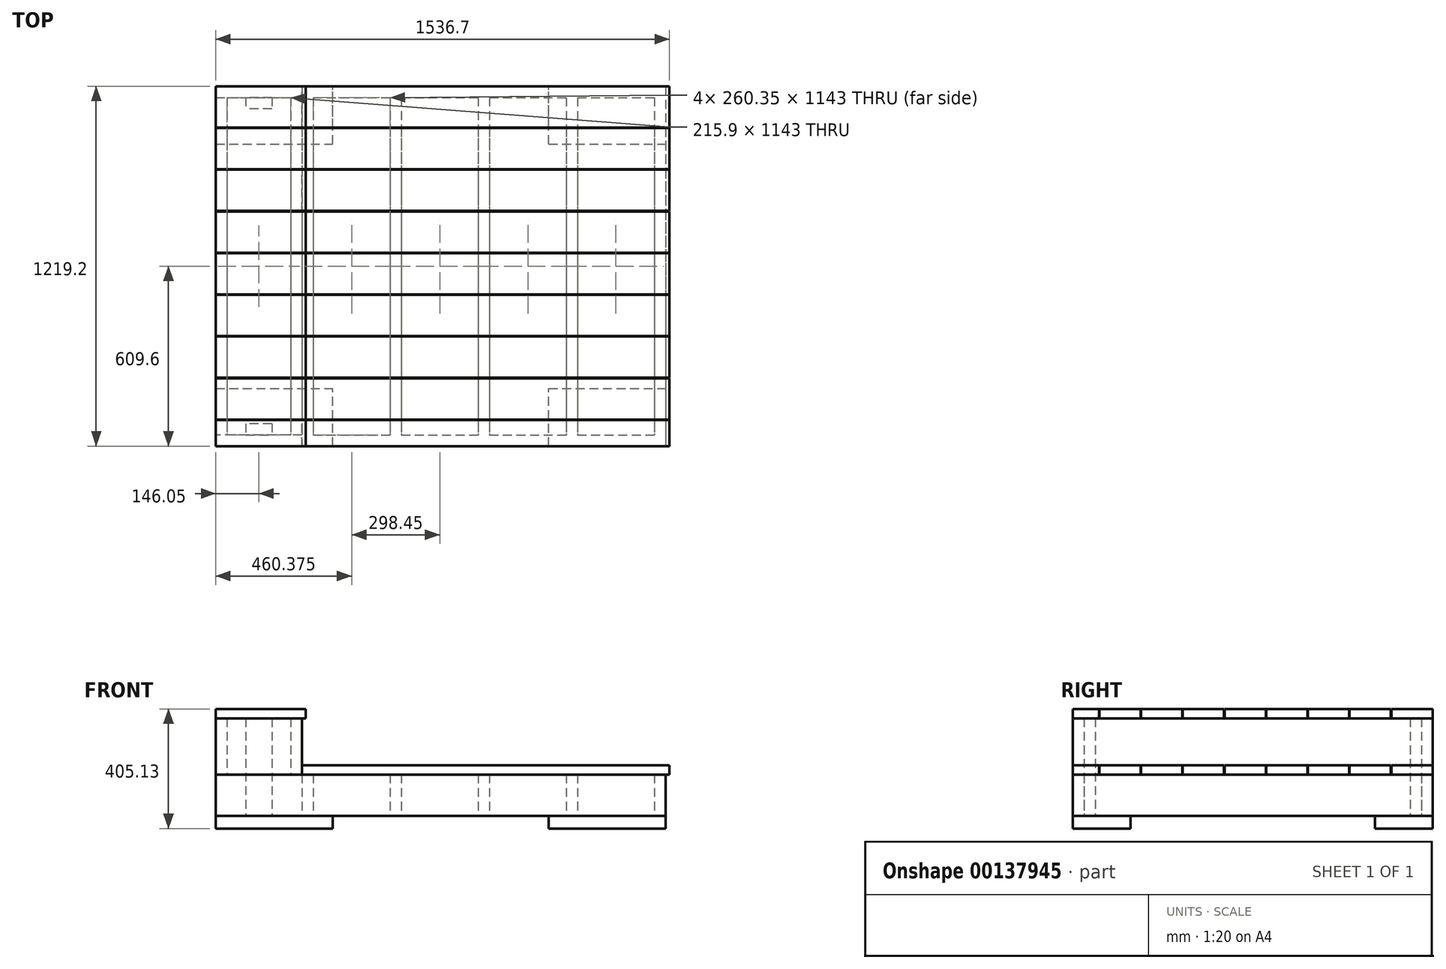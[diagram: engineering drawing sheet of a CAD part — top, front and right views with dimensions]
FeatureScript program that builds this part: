
annotation { "Feature Type Name" : "Feature", "Feature Type Description" : "" }
export const myFeature = defineFeature(function(context is Context, id is Id, definition is map)
    precondition{}
    {
        {
            var Q0;
            Q0=qCreatedBy(makeId("Top.planeOp"),FACE);
            var sketch = newSketch(context, id + "F0", { "sketchPlane" : qUnion([Q0])});
            skLineSegment(sketch, "E0.bottom", {"start": v(-762, 609.6) * mm, "end": v(762, 609.6) * mm});
            skLineSegment(sketch, "E0.top", {"start": v(-762, -609.6) * mm, "end": v(762, -609.6) * mm});
            skLineSegment(sketch, "E0.left", {"start": v(-762, 609.6) * mm, "end": v(-762, 571.5) * mm});
            skLineSegment(sketch, "E0.right", {"start": v(762, 609.6) * mm, "end": v(762, -609.6) * mm});
            skLineSegment(sketch, "E1.bottom", {"start": v(-431.8, 571.5) * mm, "end": v(-171.45, 571.5) * mm});
            skLineSegment(sketch, "E1.top", {"start": v(-431.8, -571.5) * mm, "end": v(-171.45, -571.5) * mm});
            skLineSegment(sketch, "E1.left", {"start": v(-431.8, 571.5) * mm, "end": v(-431.8, -571.5) * mm});
            skLineSegment(sketch, "E1.right", {"start": v(-171.45, 571.5) * mm, "end": v(-171.45, -571.5) * mm});
            skLineSegment(sketch, "E2.bottom", {"start": v(-133.35, 571.5) * mm, "end": v(127, 571.5) * mm});
            skLineSegment(sketch, "E2.top", {"start": v(-133.35, -571.5) * mm, "end": v(127, -571.5) * mm});
            skLineSegment(sketch, "E2.left", {"start": v(-133.35, 571.5) * mm, "end": v(-133.35, -571.5) * mm});
            skLineSegment(sketch, "E2.right", {"start": v(127, 571.5) * mm, "end": v(127, -571.5) * mm});
            skLineSegment(sketch, "E3.bottom", {"start": v(165.1, 571.5) * mm, "end": v(425.45, 571.5) * mm});
            skLineSegment(sketch, "E3.top", {"start": v(165.1, -571.5) * mm, "end": v(425.45, -571.5) * mm});
            skLineSegment(sketch, "E3.left", {"start": v(165.1, 571.5) * mm, "end": v(165.1, -571.5) * mm});
            skLineSegment(sketch, "E3.right", {"start": v(425.45, 571.5) * mm, "end": v(425.45, -571.5) * mm});
            skLineSegment(sketch, "E4.bottom", {"start": v(463.55, 571.5) * mm, "end": v(723.9, 571.5) * mm});
            skLineSegment(sketch, "E4.top", {"start": v(463.55, -571.5) * mm, "end": v(723.9, -571.5) * mm});
            skLineSegment(sketch, "E4.left", {"start": v(463.55, 571.5) * mm, "end": v(463.55, -571.5) * mm});
            skLineSegment(sketch, "E4.right", {"start": v(723.9, 571.5) * mm, "end": v(723.9, -571.5) * mm});
            skLineSegment(sketch, "E5", {"start": v(-762, 571.5) * mm, "end": v(-469.9, 571.5) * mm});
            skLineSegment(sketch, "E6", {"start": v(-469.9, 571.5) * mm, "end": v(-469.9, -571.5) * mm});
            skLineSegment(sketch, "E7", {"start": v(-469.9, -571.5) * mm, "end": v(-762, -571.5) * mm});
            skLineSegment(sketch, "E8.trimOffspring", {"start": v(-762, -571.5) * mm, "end": v(-762, -609.6) * mm});
            skLineSegment(sketch, "E9", {"start": v(-762, -609.6) * mm, "end": v(762, 609.6) * mm, "construction": true});
            skLineSegment(sketch, "E10", {"start": v(-762, 609.6) * mm, "end": v(762, -609.6) * mm, "construction": true});
            skSolve(sketch);
        }
        {
            var Q0;
            Q0=makeQuery(id+"F0.imprint","IMPRINT",FACE,{"disambiguationData":[TD([[makeQuery(id+"F0.imprint","IMPRINT",EDGE,{"derivedFrom":sQuery(id+"F0.wireOp",EDGE,"E0.bottom")}),-1.0]])]});
            extrude(context, id + "F1", {"entities" : qUnion([Q0]), "depth" : 139.7 * mm});
        }
        {
            var Q0;
            Q0=makeQuery(id+"F1.opExtrude","CAP_FACE",FACE,{"disambiguationData":[OSD([sQuery(id+"F0.wireOp",EDGE,"E0.bottom"),sQuery(id+"F0.wireOp",EDGE,"E0.top"),sQuery(id+"F0.wireOp",EDGE,"E0.left"),sQuery(id+"F0.wireOp",EDGE,"E0.right"),sQuery(id+"F0.wireOp",EDGE,"E1.bottom"),sQuery(id+"F0.wireOp",EDGE,"E1.top"),sQuery(id+"F0.wireOp",EDGE,"E1.left"),sQuery(id+"F0.wireOp",EDGE,"E1.right"),sQuery(id+"F0.wireOp",EDGE,"E2.bottom"),sQuery(id+"F0.wireOp",EDGE,"E2.top"),sQuery(id+"F0.wireOp",EDGE,"E2.left"),sQuery(id+"F0.wireOp",EDGE,"E2.right"),sQuery(id+"F0.wireOp",EDGE,"E3.bottom"),sQuery(id+"F0.wireOp",EDGE,"E3.top"),sQuery(id+"F0.wireOp",EDGE,"E3.left"),sQuery(id+"F0.wireOp",EDGE,"E3.right"),sQuery(id+"F0.wireOp",EDGE,"E4.bottom"),sQuery(id+"F0.wireOp",EDGE,"E4.top"),sQuery(id+"F0.wireOp",EDGE,"E4.left"),sQuery(id+"F0.wireOp",EDGE,"E4.right"),sQuery(id+"F0.wireOp",EDGE,"E5"),sQuery(id+"F0.wireOp",EDGE,"E6"),sQuery(id+"F0.wireOp",EDGE,"E7"),sQuery(id+"F0.wireOp",EDGE,"E8.trimOffspring")])],"isStart":false});
            var sketch = newSketch(context, id + "F2", { "sketchPlane" : qUnion([Q0])});
            skLineSegment(sketch, "E11.top", {"start": v(-762, -609.6) * mm, "end": v(-469.9, -609.6) * mm});
            skLineSegment(sketch, "E11.left", {"start": v(-762, 609.6) * mm, "end": v(-762, -609.6) * mm});
            skLineSegment(sketch, "E11.right", {"start": v(-469.9, 609.6) * mm, "end": v(-469.9, -609.6) * mm});
            skLineSegment(sketch, "E12.bottom", {"start": v(-723.9, 571.5) * mm, "end": v(-508, 571.5) * mm});
            skLineSegment(sketch, "E12.top", {"start": v(-723.9, -571.5) * mm, "end": v(-508, -571.5) * mm});
            skLineSegment(sketch, "E12.left", {"start": v(-723.9, 571.5) * mm, "end": v(-723.9, -571.5) * mm});
            skLineSegment(sketch, "E12.right", {"start": v(-508, 571.5) * mm, "end": v(-508, -571.5) * mm});
            skLineSegment(sketch, "E13", {"start": v(-762, 609.6) * mm, "end": v(-469.9, 609.6) * mm});
            skSolve(sketch);
        }
        {
            var Q0;
            {var subQ9=sQuery(id+"F2.wireOp",EDGE,"E11.top");Q0=makeQuery(id+"F2.imprint","IMPRINT",FACE,{"disambiguationData":[TD([[makeQuery(id+"F2.imprint","IMPRINT",EDGE,{"derivedFrom":subQ9}),1.0]])]});}
            var Q1;
            {var subQ0=sQuery(id+"F2.wireOp",EDGE,"E12.right");Q1=makeQuery(id+"F2.imprint","IMPRINT",FACE,{"disambiguationData":[TD([[makeQuery(id+"F2.imprint","IMPRINT",EDGE,{"derivedFrom":subQ0}),1.0]])]});}
            var Q2;
            {var subQ1=makeQuery(id+"F1.opExtrude","CAP_EDGE",EDGE,{"disambiguationData":[OSD([sQuery(id+"F0.wireOp",EDGE,"E0.left")])],"isStart":false});Q2=makeQuery(id+"F2.imprint","IMPRINT",FACE,{"disambiguationData":[TD([[makeQuery(id+"F2.imprint","IMPRINT",EDGE,{"derivedFrom":subQ1}),1.0]])]});}
            var Q3;
            {var subQ1=makeQuery(id+"F1.opExtrude","CAP_EDGE",EDGE,{"disambiguationData":[OSD([sQuery(id+"F0.wireOp",EDGE,"E7")])],"isStart":false});Q3=makeQuery(id+"F2.imprint","IMPRINT",FACE,{"disambiguationData":[TD([[makeQuery(id+"F2.imprint","IMPRINT",EDGE,{"derivedFrom":subQ1}),1.0]])]});}
            var Q4;
            {var subQ5=sQuery(id+"F2.wireOp",EDGE,"E12.left");Q4=makeQuery(id+"F2.imprint","IMPRINT",FACE,{"disambiguationData":[TD([[makeQuery(id+"F2.imprint","IMPRINT",EDGE,{"derivedFrom":subQ5}),-1.0]])]});}
            var Q5;
            {var subQ0=sQuery(id+"F2.wireOp",EDGE,"E12.bottom");Q5=makeQuery(id+"F2.imprint","IMPRINT",FACE,{"disambiguationData":[TD([[makeQuery(id+"F2.imprint","IMPRINT",EDGE,{"derivedFrom":subQ0}),1.0]])]});}
            extrude(context, id + "F3", {"entities" : qUnion([Q0, Q1, Q2, Q3, Q4, Q5]), "depth" : 190.5 * mm});
        }
        {
            var Q0;
            Q0=makeQuery(id+"F3.opExtrude","SWEPT_FACE",FACE,{"disambiguationData":[OSD([sQuery(id+"F2.wireOp",EDGE,"E11.left")])]});
            var sketch = newSketch(context, id + "F4", { "sketchPlane" : qUnion([Q0])});
            skLineSegment(sketch, "E14.bottom", {"start": v(-609.6, 361.95) * mm, "end": v(-469.9, 361.95) * mm});
            skLineSegment(sketch, "E14.top", {"start": v(-609.6, 330.2) * mm, "end": v(-469.9, 330.2) * mm});
            skLineSegment(sketch, "E14.left", {"start": v(-609.6, 361.95) * mm, "end": v(-609.6, 330.2) * mm});
            skLineSegment(sketch, "E14.right", {"start": v(-469.9, 361.95) * mm, "end": v(-469.9, 330.2) * mm});
            skLineSegment(sketch, "E15.bottom", {"start": v(-468.31, 361.95) * mm, "end": v(-328.61, 361.95) * mm});
            skLineSegment(sketch, "E15.top", {"start": v(-468.31, 330.2) * mm, "end": v(-328.61, 330.2) * mm});
            skLineSegment(sketch, "E15.left", {"start": v(-468.31, 361.95) * mm, "end": v(-468.31, 330.2) * mm});
            skLineSegment(sketch, "E15.right", {"start": v(-328.61, 361.95) * mm, "end": v(-328.61, 330.2) * mm});
            skLineSegment(sketch, "E16.bottom", {"start": v(379.41, 361.95) * mm, "end": v(519.11, 361.95) * mm});
            skLineSegment(sketch, "E16.top", {"start": v(379.41, 330.2) * mm, "end": v(519.11, 330.2) * mm});
            skLineSegment(sketch, "E16.left", {"start": v(379.41, 361.95) * mm, "end": v(379.41, 330.2) * mm});
            skLineSegment(sketch, "E16.right", {"start": v(519.11, 361.95) * mm, "end": v(519.11, 330.2) * mm});
            skLineSegment(sketch, "E17.bottom", {"start": v(-327.03, 361.95) * mm, "end": v(-187.32, 361.95) * mm});
            skLineSegment(sketch, "E17.top", {"start": v(-327.03, 330.2) * mm, "end": v(-187.32, 330.2) * mm});
            skLineSegment(sketch, "E17.left", {"start": v(-327.03, 361.95) * mm, "end": v(-327.03, 330.2) * mm});
            skLineSegment(sketch, "E17.right", {"start": v(-187.32, 361.95) * mm, "end": v(-187.32, 330.2) * mm});
            skLineSegment(sketch, "E18.bottom", {"start": v(-185.74, 361.95) * mm, "end": v(-46.04, 361.95) * mm});
            skLineSegment(sketch, "E18.top", {"start": v(-185.74, 330.2) * mm, "end": v(-46.04, 330.2) * mm});
            skLineSegment(sketch, "E18.left", {"start": v(-185.74, 361.95) * mm, "end": v(-185.74, 330.2) * mm});
            skLineSegment(sketch, "E18.right", {"start": v(-46.04, 361.95) * mm, "end": v(-46.04, 330.2) * mm});
            skLineSegment(sketch, "E19.bottom", {"start": v(-44.45, 361.95) * mm, "end": v(95.25, 361.95) * mm});
            skLineSegment(sketch, "E19.top", {"start": v(-44.45, 330.2) * mm, "end": v(95.25, 330.2) * mm});
            skLineSegment(sketch, "E19.left", {"start": v(-44.45, 361.95) * mm, "end": v(-44.45, 330.2) * mm});
            skLineSegment(sketch, "E19.right", {"start": v(95.25, 361.95) * mm, "end": v(95.25, 330.2) * mm});
            skLineSegment(sketch, "E20.bottom", {"start": v(96.84, 361.95) * mm, "end": v(236.54, 361.95) * mm});
            skLineSegment(sketch, "E20.top", {"start": v(96.84, 330.2) * mm, "end": v(236.54, 330.2) * mm});
            skLineSegment(sketch, "E20.left", {"start": v(96.84, 361.95) * mm, "end": v(96.84, 330.2) * mm});
            skLineSegment(sketch, "E20.right", {"start": v(236.54, 361.95) * mm, "end": v(236.54, 330.2) * mm});
            skLineSegment(sketch, "E21.bottom", {"start": v(238.13, 361.95) * mm, "end": v(377.83, 361.95) * mm});
            skLineSegment(sketch, "E21.top", {"start": v(238.13, 330.2) * mm, "end": v(377.83, 330.2) * mm});
            skLineSegment(sketch, "E21.left", {"start": v(238.13, 361.95) * mm, "end": v(238.13, 330.2) * mm});
            skLineSegment(sketch, "E21.right", {"start": v(377.83, 361.95) * mm, "end": v(377.83, 330.2) * mm});
            skLineSegment(sketch, "E22.bottom", {"start": v(520.7, 361.95) * mm, "end": v(609.6, 361.95) * mm});
            skLineSegment(sketch, "E22.top", {"start": v(520.7, 330.2) * mm, "end": v(609.6, 330.2) * mm});
            skLineSegment(sketch, "E22.left", {"start": v(520.7, 361.95) * mm, "end": v(520.7, 330.2) * mm});
            skLineSegment(sketch, "E22.right", {"start": v(609.6, 361.95) * mm, "end": v(609.6, 330.2) * mm});
            skSolve(sketch);
        }
        {
            var Q0;
            Q0=makeQuery(id+"F4.imprint","IMPRINT",FACE,{"disambiguationData":[TD([[makeQuery(id+"F4.imprint","IMPRINT",EDGE,{"derivedFrom":sQuery(id+"F4.wireOp",EDGE,"E14.bottom")}),-1.0]])]});
            var Q1;
            Q1=makeQuery(id+"F4.imprint","IMPRINT",FACE,{"disambiguationData":[TD([[makeQuery(id+"F4.imprint","IMPRINT",EDGE,{"derivedFrom":sQuery(id+"F4.wireOp",EDGE,"E15.bottom")}),-1.0]])]});
            var Q2;
            Q2=makeQuery(id+"F4.imprint","IMPRINT",FACE,{"disambiguationData":[TD([[makeQuery(id+"F4.imprint","IMPRINT",EDGE,{"derivedFrom":sQuery(id+"F4.wireOp",EDGE,"E17.bottom")}),-1.0]])]});
            var Q3;
            Q3=makeQuery(id+"F4.imprint","IMPRINT",FACE,{"disambiguationData":[TD([[makeQuery(id+"F4.imprint","IMPRINT",EDGE,{"derivedFrom":sQuery(id+"F4.wireOp",EDGE,"E18.bottom")}),-1.0]])]});
            var Q4;
            Q4=makeQuery(id+"F4.imprint","IMPRINT",FACE,{"disambiguationData":[TD([[makeQuery(id+"F4.imprint","IMPRINT",EDGE,{"derivedFrom":sQuery(id+"F4.wireOp",EDGE,"E19.bottom")}),-1.0]])]});
            var Q5;
            Q5=makeQuery(id+"F4.imprint","IMPRINT",FACE,{"disambiguationData":[TD([[makeQuery(id+"F4.imprint","IMPRINT",EDGE,{"derivedFrom":sQuery(id+"F4.wireOp",EDGE,"E20.bottom")}),-1.0]])]});
            var Q6;
            Q6=makeQuery(id+"F4.imprint","IMPRINT",FACE,{"disambiguationData":[TD([[makeQuery(id+"F4.imprint","IMPRINT",EDGE,{"derivedFrom":sQuery(id+"F4.wireOp",EDGE,"E21.bottom")}),-1.0]])]});
            var Q7;
            Q7=makeQuery(id+"F4.imprint","IMPRINT",FACE,{"disambiguationData":[TD([[makeQuery(id+"F4.imprint","IMPRINT",EDGE,{"derivedFrom":sQuery(id+"F4.wireOp",EDGE,"E16.bottom")}),-1.0]])]});
            var Q8;
            Q8=makeQuery(id+"F4.imprint","IMPRINT",FACE,{"disambiguationData":[TD([[makeQuery(id+"F4.imprint","IMPRINT",EDGE,{"derivedFrom":sQuery(id+"F4.wireOp",EDGE,"E22.bottom")}),-1.0]])]});
            extrude(context, id + "F5", {"entities" : qUnion([Q0, Q1, Q2, Q3, Q4, Q5, Q6, Q7, Q8]), "oppositeDirection" : true, "depth" : 304.8 * mm});
        }
        {
            var Q0;
            Q0=makeQuery(id+"F3.opExtrude","SWEPT_FACE",FACE,{"disambiguationData":[OSD([sQuery(id+"F2.wireOp",EDGE,"E11.right")])]});
            var sketch = newSketch(context, id + "F6", { "sketchPlane" : qUnion([Q0])});
            skLineSegment(sketch, "E23.bottom", {"start": v(-609.6, 171.45) * mm, "end": v(-520.7, 171.45) * mm});
            skLineSegment(sketch, "E23.top", {"start": v(-609.6, 139.7) * mm, "end": v(-520.7, 139.7) * mm});
            skLineSegment(sketch, "E23.left", {"start": v(-609.6, 171.45) * mm, "end": v(-609.6, 139.7) * mm});
            skLineSegment(sketch, "E23.right", {"start": v(-520.7, 171.45) * mm, "end": v(-520.7, 139.7) * mm});
            skLineSegment(sketch, "E24.bottom", {"start": v(187.32, 171.45) * mm, "end": v(327.02, 171.45) * mm});
            skLineSegment(sketch, "E24.top", {"start": v(187.32, 139.7) * mm, "end": v(327.02, 139.7) * mm});
            skLineSegment(sketch, "E24.left", {"start": v(187.32, 171.45) * mm, "end": v(187.32, 139.7) * mm});
            skLineSegment(sketch, "E24.right", {"start": v(327.02, 171.45) * mm, "end": v(327.02, 139.7) * mm});
            skLineSegment(sketch, "E25.bottom", {"start": v(328.61, 171.45) * mm, "end": v(468.31, 171.45) * mm});
            skLineSegment(sketch, "E25.top", {"start": v(328.61, 139.7) * mm, "end": v(468.31, 139.7) * mm});
            skLineSegment(sketch, "E25.left", {"start": v(328.61, 171.45) * mm, "end": v(328.61, 139.7) * mm});
            skLineSegment(sketch, "E25.right", {"start": v(468.31, 171.45) * mm, "end": v(468.31, 139.7) * mm});
            skLineSegment(sketch, "E26.bottom", {"start": v(-519.11, 171.45) * mm, "end": v(-379.41, 171.45) * mm});
            skLineSegment(sketch, "E26.top", {"start": v(-519.11, 139.7) * mm, "end": v(-379.41, 139.7) * mm});
            skLineSegment(sketch, "E26.left", {"start": v(-519.11, 171.45) * mm, "end": v(-519.11, 139.7) * mm});
            skLineSegment(sketch, "E26.right", {"start": v(-379.41, 171.45) * mm, "end": v(-379.41, 139.7) * mm});
            skLineSegment(sketch, "E27.bottom", {"start": v(-377.83, 171.45) * mm, "end": v(-238.13, 171.45) * mm});
            skLineSegment(sketch, "E27.top", {"start": v(-377.83, 139.7) * mm, "end": v(-238.13, 139.7) * mm});
            skLineSegment(sketch, "E27.left", {"start": v(-377.83, 171.45) * mm, "end": v(-377.83, 139.7) * mm});
            skLineSegment(sketch, "E27.right", {"start": v(-238.13, 171.45) * mm, "end": v(-238.13, 139.7) * mm});
            skLineSegment(sketch, "E28.bottom", {"start": v(-236.54, 171.45) * mm, "end": v(-96.84, 171.45) * mm});
            skLineSegment(sketch, "E28.top", {"start": v(-236.54, 139.7) * mm, "end": v(-96.84, 139.7) * mm});
            skLineSegment(sketch, "E28.left", {"start": v(-236.54, 171.45) * mm, "end": v(-236.54, 139.7) * mm});
            skLineSegment(sketch, "E28.right", {"start": v(-96.84, 171.45) * mm, "end": v(-96.84, 139.7) * mm});
            skLineSegment(sketch, "E29.bottom", {"start": v(-95.25, 171.45) * mm, "end": v(44.45, 171.45) * mm});
            skLineSegment(sketch, "E29.top", {"start": v(-95.25, 139.7) * mm, "end": v(44.45, 139.7) * mm});
            skLineSegment(sketch, "E29.left", {"start": v(-95.25, 171.45) * mm, "end": v(-95.25, 139.7) * mm});
            skLineSegment(sketch, "E29.right", {"start": v(44.45, 171.45) * mm, "end": v(44.45, 139.7) * mm});
            skLineSegment(sketch, "E30.bottom", {"start": v(46.04, 171.45) * mm, "end": v(185.74, 171.45) * mm});
            skLineSegment(sketch, "E30.top", {"start": v(46.04, 139.7) * mm, "end": v(185.74, 139.7) * mm});
            skLineSegment(sketch, "E30.left", {"start": v(46.04, 171.45) * mm, "end": v(46.04, 139.7) * mm});
            skLineSegment(sketch, "E30.right", {"start": v(185.74, 171.45) * mm, "end": v(185.74, 139.7) * mm});
            skLineSegment(sketch, "E31.bottom", {"start": v(469.9, 171.45) * mm, "end": v(609.6, 171.45) * mm});
            skLineSegment(sketch, "E31.top", {"start": v(469.9, 139.7) * mm, "end": v(609.6, 139.7) * mm});
            skLineSegment(sketch, "E31.left", {"start": v(469.9, 171.45) * mm, "end": v(469.9, 139.7) * mm});
            skLineSegment(sketch, "E31.right", {"start": v(609.6, 171.45) * mm, "end": v(609.6, 139.7) * mm});
            skSolve(sketch);
        }
        {
            var Q0;
            Q0=makeQuery(id+"F6.imprint","IMPRINT",FACE,{"disambiguationData":[TD([[makeQuery(id+"F6.imprint","IMPRINT",EDGE,{"derivedFrom":sQuery(id+"F6.wireOp",EDGE,"E23.bottom")}),-1.0]])]});
            var Q1;
            Q1=makeQuery(id+"F6.imprint","IMPRINT",FACE,{"disambiguationData":[TD([[makeQuery(id+"F6.imprint","IMPRINT",EDGE,{"derivedFrom":sQuery(id+"F6.wireOp",EDGE,"E26.bottom")}),-1.0]])]});
            var Q2;
            Q2=makeQuery(id+"F6.imprint","IMPRINT",FACE,{"disambiguationData":[TD([[makeQuery(id+"F6.imprint","IMPRINT",EDGE,{"derivedFrom":sQuery(id+"F6.wireOp",EDGE,"E27.bottom")}),-1.0]])]});
            var Q3;
            Q3=makeQuery(id+"F6.imprint","IMPRINT",FACE,{"disambiguationData":[TD([[makeQuery(id+"F6.imprint","IMPRINT",EDGE,{"derivedFrom":sQuery(id+"F6.wireOp",EDGE,"E28.bottom")}),-1.0]])]});
            var Q4;
            Q4=makeQuery(id+"F6.imprint","IMPRINT",FACE,{"disambiguationData":[TD([[makeQuery(id+"F6.imprint","IMPRINT",EDGE,{"derivedFrom":sQuery(id+"F6.wireOp",EDGE,"E29.bottom")}),-1.0]])]});
            var Q5;
            Q5=makeQuery(id+"F6.imprint","IMPRINT",FACE,{"disambiguationData":[TD([[makeQuery(id+"F6.imprint","IMPRINT",EDGE,{"derivedFrom":sQuery(id+"F6.wireOp",EDGE,"E30.bottom")}),-1.0]])]});
            var Q6;
            Q6=makeQuery(id+"F6.imprint","IMPRINT",FACE,{"disambiguationData":[TD([[makeQuery(id+"F6.imprint","IMPRINT",EDGE,{"derivedFrom":sQuery(id+"F6.wireOp",EDGE,"E24.bottom")}),-1.0]])]});
            var Q7;
            Q7=makeQuery(id+"F6.imprint","IMPRINT",FACE,{"disambiguationData":[TD([[makeQuery(id+"F6.imprint","IMPRINT",EDGE,{"derivedFrom":sQuery(id+"F6.wireOp",EDGE,"E25.bottom")}),-1.0]])]});
            var Q8;
            Q8=makeQuery(id+"F6.imprint","IMPRINT",FACE,{"disambiguationData":[TD([[makeQuery(id+"F6.imprint","IMPRINT",EDGE,{"derivedFrom":sQuery(id+"F6.wireOp",EDGE,"E31.bottom")}),-1.0]])]});
            extrude(context, id + "F7", {"entities" : qUnion([Q0, Q1, Q2, Q3, Q4, Q5, Q6, Q7, Q8]), "depth" : 1244.6 * mm});
        }
        {
            var Q0;
            Q0=makeQuery(id+"F1.opExtrude","CAP_FACE",FACE,{"disambiguationData":[OSD([sQuery(id+"F0.wireOp",EDGE,"E0.bottom"),sQuery(id+"F0.wireOp",EDGE,"E0.top"),sQuery(id+"F0.wireOp",EDGE,"E0.left"),sQuery(id+"F0.wireOp",EDGE,"E0.right"),sQuery(id+"F0.wireOp",EDGE,"E1.bottom"),sQuery(id+"F0.wireOp",EDGE,"E1.top"),sQuery(id+"F0.wireOp",EDGE,"E1.left"),sQuery(id+"F0.wireOp",EDGE,"E1.right"),sQuery(id+"F0.wireOp",EDGE,"E2.bottom"),sQuery(id+"F0.wireOp",EDGE,"E2.top"),sQuery(id+"F0.wireOp",EDGE,"E2.left"),sQuery(id+"F0.wireOp",EDGE,"E2.right"),sQuery(id+"F0.wireOp",EDGE,"E3.bottom"),sQuery(id+"F0.wireOp",EDGE,"E3.top"),sQuery(id+"F0.wireOp",EDGE,"E3.left"),sQuery(id+"F0.wireOp",EDGE,"E3.right"),sQuery(id+"F0.wireOp",EDGE,"E4.bottom"),sQuery(id+"F0.wireOp",EDGE,"E4.top"),sQuery(id+"F0.wireOp",EDGE,"E4.left"),sQuery(id+"F0.wireOp",EDGE,"E4.right"),sQuery(id+"F0.wireOp",EDGE,"E5"),sQuery(id+"F0.wireOp",EDGE,"E6"),sQuery(id+"F0.wireOp",EDGE,"E7"),sQuery(id+"F0.wireOp",EDGE,"E8.trimOffspring")])],"isStart":true});
            var sketch = newSketch(context, id + "F8", { "sketchPlane" : qUnion([Q0])});
            skLineSegment(sketch, "E32.bottom", {"start": v(-660.4, 571.5) * mm, "end": v(-571.5, 571.5) * mm});
            skLineSegment(sketch, "E32.top", {"start": v(-660.4, 533.4) * mm, "end": v(-571.5, 533.4) * mm});
            skLineSegment(sketch, "E32.left", {"start": v(-660.4, 571.5) * mm, "end": v(-660.4, 533.4) * mm});
            skLineSegment(sketch, "E32.right", {"start": v(-571.5, 571.5) * mm, "end": v(-571.5, 533.4) * mm});
            skLineSegment(sketch, "E33.bottom", {"start": v(-660.4, -533.4) * mm, "end": v(-571.5, -533.4) * mm});
            skLineSegment(sketch, "E33.top", {"start": v(-660.4, -571.5) * mm, "end": v(-571.5, -571.5) * mm});
            skLineSegment(sketch, "E33.left", {"start": v(-660.4, -533.4) * mm, "end": v(-660.4, -571.5) * mm});
            skLineSegment(sketch, "E33.right", {"start": v(-571.5, -533.4) * mm, "end": v(-571.5, -571.5) * mm});
            skSolve(sketch);
        }
        {
            var Q0;
            Q0=makeQuery(id+"F8.imprint","IMPRINT",FACE,{"disambiguationData":[TD([[makeQuery(id+"F8.imprint","IMPRINT",EDGE,{"derivedFrom":sQuery(id+"F8.wireOp",EDGE,"E32.bottom")}),1.0]])]});
            var Q1;
            Q1=makeQuery(id+"F8.imprint","IMPRINT",FACE,{"disambiguationData":[TD([[makeQuery(id+"F8.imprint","IMPRINT",EDGE,{"derivedFrom":sQuery(id+"F8.wireOp",EDGE,"E33.bottom")}),-1.0]])]});
            extrude(context, id + "F9", {"entities" : qUnion([Q0, Q1]), "endBound" : BoundingType.UP_TO_NEXT, "oppositeDirection" : true, "depth" : 25.4 * mm});
        }
        {
            var Q0;
            Q0=makeQuery(id+"F1.opExtrude","CAP_FACE",FACE,{"disambiguationData":[OSD([sQuery(id+"F0.wireOp",EDGE,"E0.bottom"),sQuery(id+"F0.wireOp",EDGE,"E0.top"),sQuery(id+"F0.wireOp",EDGE,"E0.left"),sQuery(id+"F0.wireOp",EDGE,"E0.right"),sQuery(id+"F0.wireOp",EDGE,"E1.bottom"),sQuery(id+"F0.wireOp",EDGE,"E1.top"),sQuery(id+"F0.wireOp",EDGE,"E1.left"),sQuery(id+"F0.wireOp",EDGE,"E1.right"),sQuery(id+"F0.wireOp",EDGE,"E2.bottom"),sQuery(id+"F0.wireOp",EDGE,"E2.top"),sQuery(id+"F0.wireOp",EDGE,"E2.left"),sQuery(id+"F0.wireOp",EDGE,"E2.right"),sQuery(id+"F0.wireOp",EDGE,"E3.bottom"),sQuery(id+"F0.wireOp",EDGE,"E3.top"),sQuery(id+"F0.wireOp",EDGE,"E3.left"),sQuery(id+"F0.wireOp",EDGE,"E3.right"),sQuery(id+"F0.wireOp",EDGE,"E4.bottom"),sQuery(id+"F0.wireOp",EDGE,"E4.top"),sQuery(id+"F0.wireOp",EDGE,"E4.left"),sQuery(id+"F0.wireOp",EDGE,"E4.right"),sQuery(id+"F0.wireOp",EDGE,"E5"),sQuery(id+"F0.wireOp",EDGE,"E6"),sQuery(id+"F0.wireOp",EDGE,"E7"),sQuery(id+"F0.wireOp",EDGE,"E8.trimOffspring")])],"isStart":true});
            var sketch = newSketch(context, id + "F10", { "sketchPlane" : qUnion([Q0])});
            skLineSegment(sketch, "E34.bottom", {"start": v(-762, 609.6) * mm, "end": v(-365.76, 609.6) * mm});
            skLineSegment(sketch, "E34.top", {"start": v(-762, 414.02) * mm, "end": v(-365.76, 414.02) * mm});
            skLineSegment(sketch, "E34.left", {"start": v(-762, 609.6) * mm, "end": v(-762, 414.02) * mm});
            skLineSegment(sketch, "E34.right", {"start": v(-365.76, 609.6) * mm, "end": v(-365.76, 414.02) * mm});
            skLineSegment(sketch, "E35.bottom", {"start": v(365.76, 609.6) * mm, "end": v(762, 609.6) * mm});
            skLineSegment(sketch, "E35.top", {"start": v(365.76, 414.02) * mm, "end": v(762, 414.02) * mm});
            skLineSegment(sketch, "E35.left", {"start": v(365.76, 609.6) * mm, "end": v(365.76, 414.02) * mm});
            skLineSegment(sketch, "E35.right", {"start": v(762, 609.6) * mm, "end": v(762, 414.02) * mm});
            skLineSegment(sketch, "E36.bottom", {"start": v(-762, -414.02) * mm, "end": v(-365.76, -414.02) * mm});
            skLineSegment(sketch, "E36.top", {"start": v(-762, -609.6) * mm, "end": v(-365.76, -609.6) * mm});
            skLineSegment(sketch, "E36.left", {"start": v(-762, -414.02) * mm, "end": v(-762, -609.6) * mm});
            skLineSegment(sketch, "E36.right", {"start": v(-365.76, -414.02) * mm, "end": v(-365.76, -609.6) * mm});
            skLineSegment(sketch, "E37.bottom", {"start": v(365.76, -414.02) * mm, "end": v(762, -414.02) * mm});
            skLineSegment(sketch, "E37.top", {"start": v(365.76, -609.6) * mm, "end": v(762, -609.6) * mm});
            skLineSegment(sketch, "E37.left", {"start": v(365.76, -414.02) * mm, "end": v(365.76, -609.6) * mm});
            skLineSegment(sketch, "E37.right", {"start": v(762, -414.02) * mm, "end": v(762, -609.6) * mm});
            skSolve(sketch);
        }
        {
            var Q0;
            Q0 = qSketchRegion(id + "F10", true);
            extrude(context, id + "F11", {"entities" : qUnion([Q0]), "depth" : 43.18 * mm});
        }
    });
